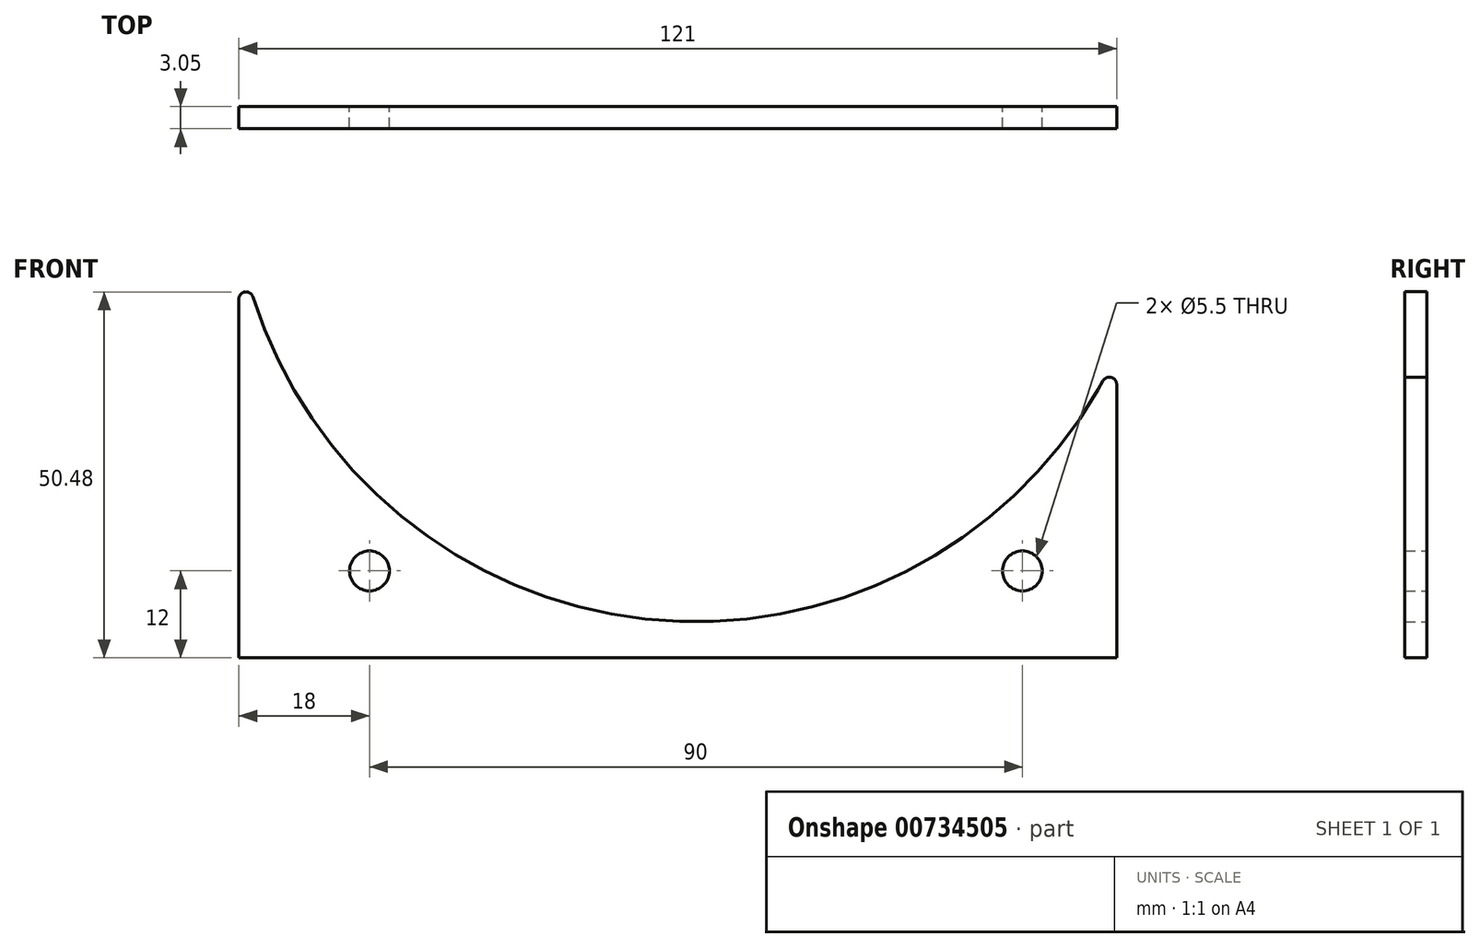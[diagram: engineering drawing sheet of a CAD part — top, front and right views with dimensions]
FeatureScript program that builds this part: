
annotation { "Feature Type Name" : "Feature", "Feature Type Description" : "" }
export const myFeature = defineFeature(function(context is Context, id is Id, definition is map)
    precondition{}
    {
        {
            var Q0;
            Q0=qCreatedBy(makeId("Front.planeOp"),FACE);
            var sketch = newSketch(context, id + "F0", { "sketchPlane" : qUnion([Q0])});
            skArc(sketch, "E0", {"start": v(58.63, 12.99) * mm, "mid": v(59.76, 13.45) * mm, "end": v(60.5, 12.49) * mm});
            skLineSegment(sketch, "E1", {"start": v(60.5, 12.49) * mm, "end": v(60.5, -25.24) * mm});
            skLineSegment(sketch, "E2", {"start": v(60.5, -25.24) * mm, "end": v(-60.5, -25.24) * mm});
            skLineSegment(sketch, "E3", {"start": v(-60.5, -25.24) * mm, "end": v(-60.5, 24.24) * mm});
            skArc(sketch, "E4", {"start": v(-60.5, 24.24) * mm, "mid": v(-59.65, 25.23) * mm, "end": v(-58.55, 24.54) * mm});
            skArc(sketch, "E5", {"start": v(-58.55, 24.54) * mm, "mid": v(-4.48, -19.86) * mm, "end": v(57.93, 11.76) * mm});
            skLineSegment(sketch, "E6", {"start": v(57.93, 11.76) * mm, "end": v(58.63, 12.99) * mm});
            skCircle(sketch, "E7", {"center": v(47.5, -13.24) * mm, "radius": 2.75 * mm});
            skCircle(sketch, "E8", {"center": v(-42.5, -13.24) * mm, "radius": 2.75 * mm});
            skLineSegment(sketch, "E9", {"start": v(-60.5, -25.24) * mm, "end": v(60.5, -25.24) * mm});
            skSolve(sketch);
        }
        {
            var Q0;
            Q0 = qSketchRegion(id + "F0", true);
            extrude(context, id + "F1", {"entities" : qUnion([Q0]), "depth" : 3.05 * mm, "offsetDistance" : 25.4 * mm});
        }
    });
